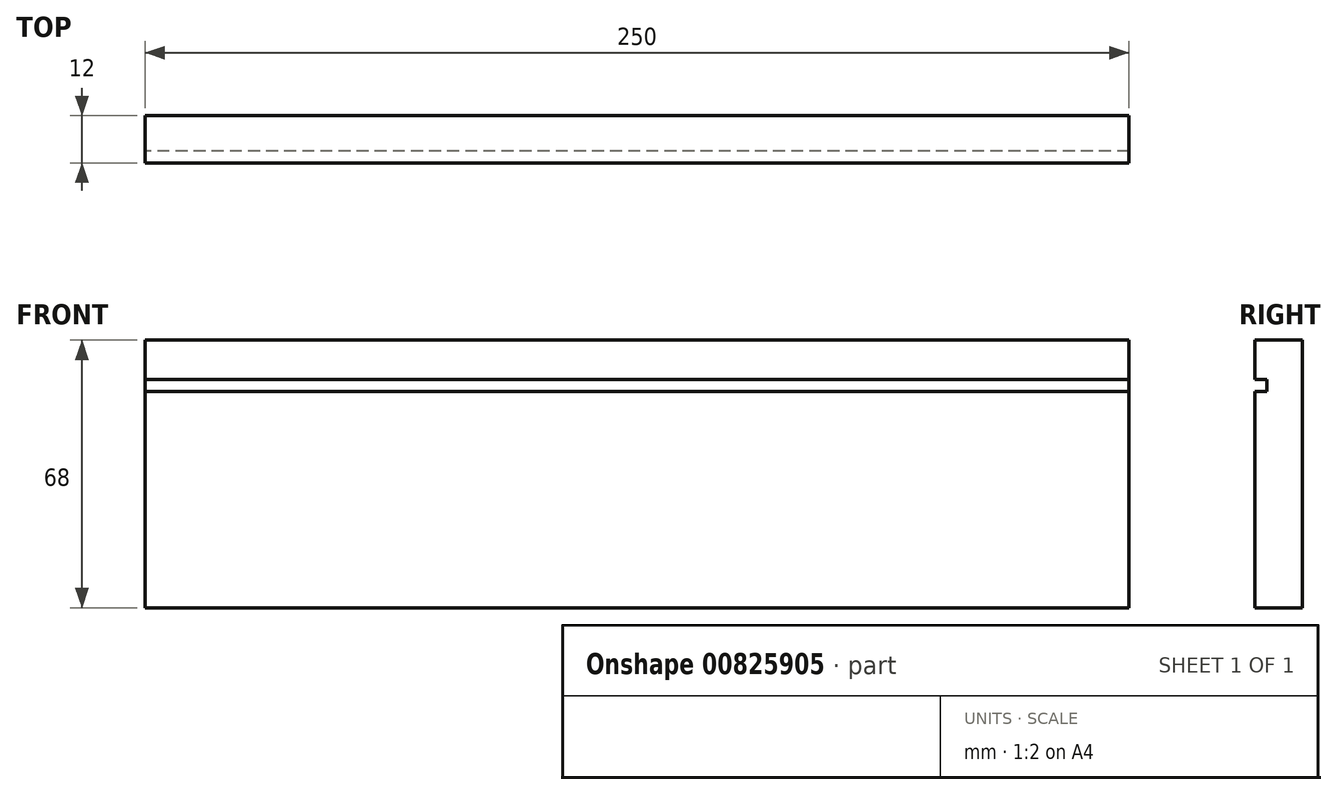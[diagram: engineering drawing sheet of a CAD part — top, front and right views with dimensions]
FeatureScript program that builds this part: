
annotation { "Feature Type Name" : "Feature", "Feature Type Description" : "" }
export const myFeature = defineFeature(function(context is Context, id is Id, definition is map)
    precondition{}
    {
        {
            var Q0;
            Q0=qCreatedBy(makeId("Right.planeOp"),FACE);
            var sketch = newSketch(context, id + "F0", { "sketchPlane" : qUnion([Q0])});
            skLineSegment(sketch, "E0.bottom", {"start": v(0, 0) * mm, "end": v(12, 0) * mm});
            skLineSegment(sketch, "E0.top", {"start": v(0, 68) * mm, "end": v(12, 68) * mm});
            skLineSegment(sketch, "E0.left", {"start": v(0, 0) * mm, "end": v(0, 55) * mm});
            skLineSegment(sketch, "E0.right", {"start": v(12, 0) * mm, "end": v(12, 68) * mm});
            skLineSegment(sketch, "E1.bottom", {"start": v(0, 55) * mm, "end": v(3, 55) * mm});
            skLineSegment(sketch, "E1.top", {"start": v(0, 58) * mm, "end": v(3, 58) * mm});
            skLineSegment(sketch, "E1.right", {"start": v(3, 55) * mm, "end": v(3, 58) * mm});
            skLineSegment(sketch, "E2", {"start": v(0, 58) * mm, "end": v(0, 68) * mm});
            skSolve(sketch);
        }
        {
            var Q0;
            Q0=makeQuery(id+"F0.imprint","IMPRINT",FACE,{"disambiguationData":[TD([[makeQuery(id+"F0.imprint","IMPRINT",EDGE,{"derivedFrom":sQuery(id+"F0.wireOp",EDGE,"E0.bottom")}),1.0]])]});
            extrude(context, id + "F1", {"entities" : qUnion([Q0]), "depth" : 250 * mm, "offsetDistance" : 25 * mm});
        }
    });
